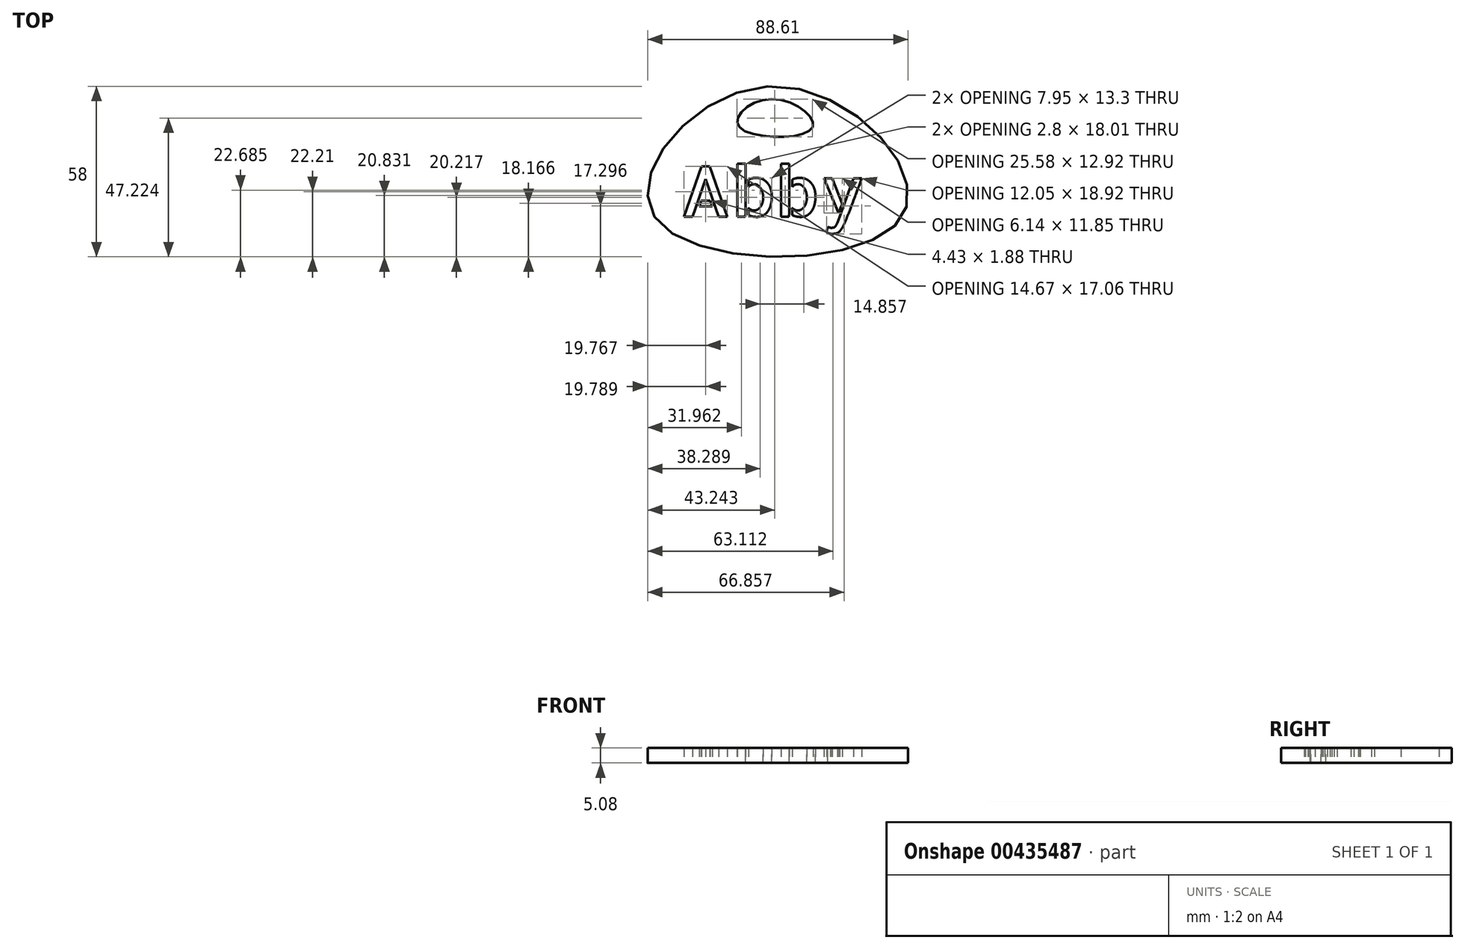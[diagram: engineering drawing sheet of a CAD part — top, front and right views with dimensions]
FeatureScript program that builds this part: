
annotation { "Feature Type Name" : "Feature", "Feature Type Description" : "" }
export const myFeature = defineFeature(function(context is Context, id is Id, definition is map)
    precondition{}
    {
        {
            var Q0;
            Q0=qCreatedBy(makeId("Top.planeOp"),FACE);
            var sketch = newSketch(context, id + "F0", { "sketchPlane" : qUnion([Q0])});
            skText(sketch, "E0", { "text": "Abby", "fontName": "AllertaStencil-Regular.ttf"});
            const initialGuessF0  = {"E0": [0, 0, 1, 0, 0.01709]};
            skSetInitialGuess(sketch, initialGuessF0);
            skSolve(sketch);
        }
        {
            var Q0;
            Q0=qCreatedBy(makeId("Top.planeOp"),FACE);
            var sketch = newSketch(context, id + "F1", { "sketchPlane" : qUnion([Q0])});
            skFitSpline(sketch, "E1", {"points": [v(-8.65, 0) * mm, v(31.7, 44.32) * mm, v(75.66, 0) * mm, v(-8.65, 0) * mm]});
            skSolve(sketch);
        }
        {
            var Q0;
            Q0=makeQuery(id+"F1.imprint","IMPRINT",FACE,{"disambiguationData":[TD([[makeQuery(id+"F1.imprint","IMPRINT",EDGE,{"derivedFrom":sQuery(id+"F1.wireOp",EDGE,"E1")}),-1.0]])]});
            extrude(context, id + "F2", {"entities" : qUnion([Q0]), "depth" : 5.08 * mm});
        }
        {
            var Q0;
            Q0 = qSketchRegion(id + "F0", true);
            extrude(context, id + "F3", {"entities" : qUnion([Q0]), "operationType" : NewBodyOperationType.REMOVE, "endBound" : BoundingType.THROUGH_ALL, "depth" : 6.35 * mm});
        }
        {
            var Q0;
            Q0=makeQuery(id+"F2.opExtrude","CAP_FACE",FACE,{"disambiguationData":[OSD([sQuery(id+"F1.wireOp",EDGE,"E1")])],"isStart":false});
            var sketch = newSketch(context, id + "F4", { "sketchPlane" : qUnion([Q0])});
            skFitSpline(sketch, "E2", {"points": [v(31.19, 40) * mm, v(20.02, 30.7) * mm, v(44.9, 30) * mm, v(31.19, 40) * mm]});
            skSolve(sketch);
        }
        {
            var Q0;
            Q0=makeQuery(id+"F4.imprint","IMPRINT",FACE,{"disambiguationData":[TD([[makeQuery(id+"F4.imprint","IMPRINT",EDGE,{"derivedFrom":sQuery(id+"F4.wireOp",EDGE,"E2")}),1.0]])]});
            extrude(context, id + "F5", {"entities" : qUnion([Q0]), "operationType" : NewBodyOperationType.REMOVE, "endBound" : BoundingType.THROUGH_ALL, "oppositeDirection" : true, "depth" : 25.4 * mm});
        }
    });
